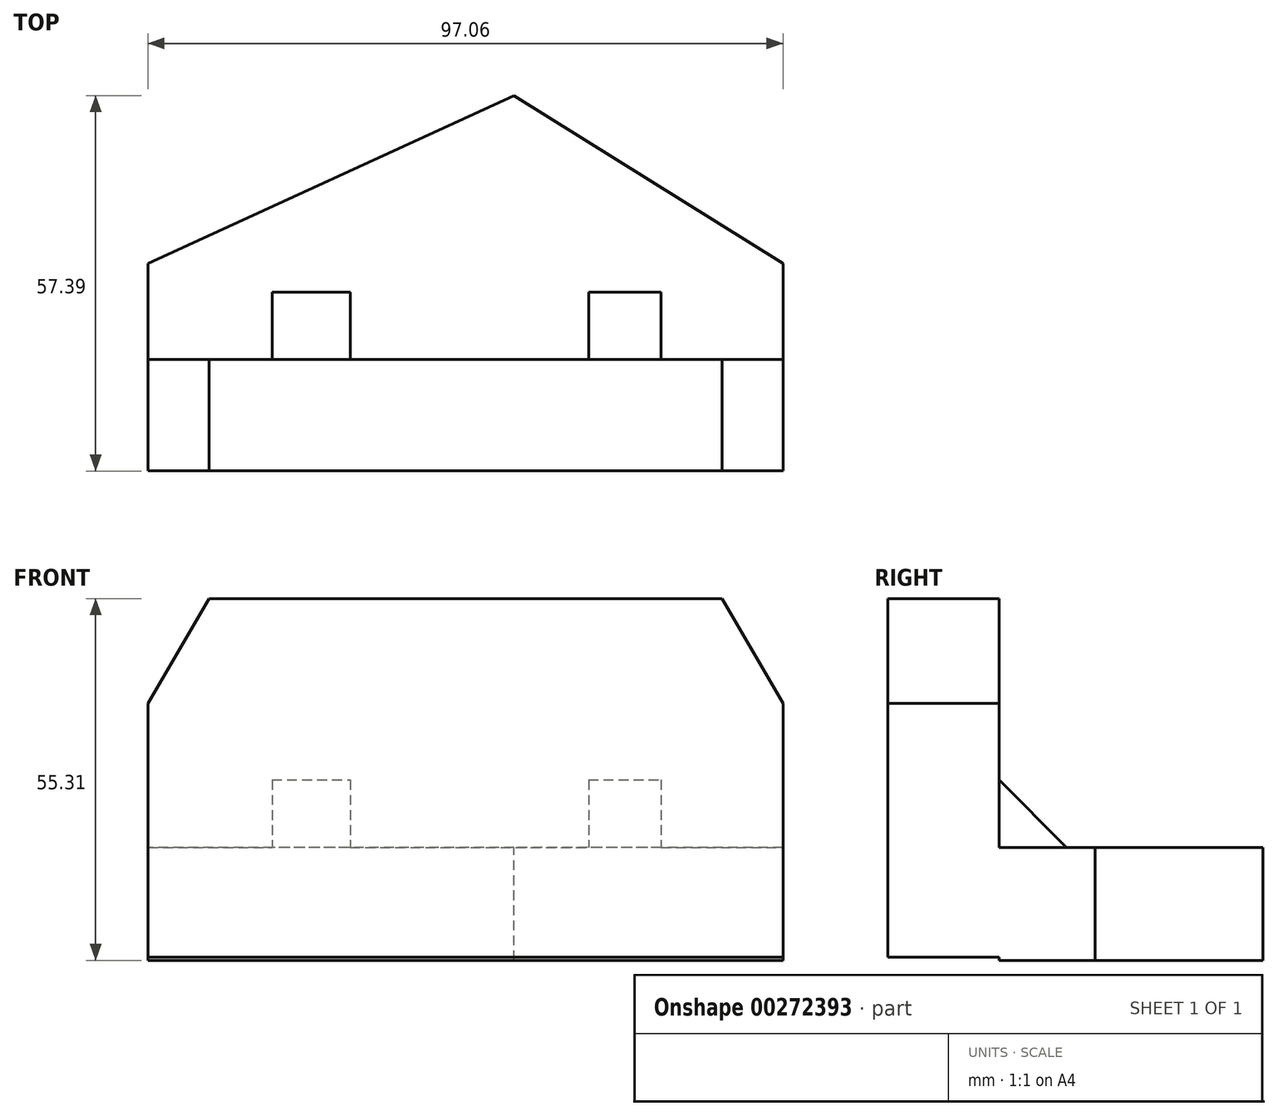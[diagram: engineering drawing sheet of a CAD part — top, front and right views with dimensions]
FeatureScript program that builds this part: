
annotation { "Feature Type Name" : "Feature", "Feature Type Description" : "" }
export const myFeature = defineFeature(function(context is Context, id is Id, definition is map)
    precondition{}
    {
        {
            var Q0;
            Q0=qCreatedBy(makeId("Front.planeOp"),FACE);
            var sketch = newSketch(context, id + "F0", { "sketchPlane" : qUnion([Q0])});
            skLineSegment(sketch, "E0", {"start": v(-58.59, -16.76) * mm, "end": v(-58.59, 22) * mm});
            skLineSegment(sketch, "E1", {"start": v(-58.59, 22) * mm, "end": v(-49.26, 38.04) * mm});
            skLineSegment(sketch, "E2", {"start": v(-49.26, 38.04) * mm, "end": v(29.15, 38.04) * mm});
            skLineSegment(sketch, "E3", {"start": v(29.15, 38.04) * mm, "end": v(38.47, 22) * mm});
            skLineSegment(sketch, "E4", {"start": v(38.47, 22) * mm, "end": v(38.47, -16.76) * mm});
            skLineSegment(sketch, "E5", {"start": v(-58.59, -16.76) * mm, "end": v(38.47, -16.76) * mm});
            skSolve(sketch);
        }
        {
            var Q0;
            Q0 = qSketchRegion(id + "F0", true);
            extrude(context, id + "F1", {"entities" : qUnion([Q0]), "depth" : 17.02 * mm});
        }
        {
            var Q0;
            Q0=qCreatedBy(makeId("Top.planeOp"),FACE);
            var sketch = newSketch(context, id + "F2", { "sketchPlane" : qUnion([Q0])});
            skLineSegment(sketch, "E6", {"start": v(-58.59, 0) * mm, "end": v(-58.59, 14.72) * mm});
            skLineSegment(sketch, "E7", {"start": v(38.47, 0) * mm, "end": v(38.47, 14.72) * mm});
            skLineSegment(sketch, "E8", {"start": v(38.47, 14.72) * mm, "end": v(-2.62, 40.37) * mm});
            skLineSegment(sketch, "E9", {"start": v(-2.62, 40.37) * mm, "end": v(-58.59, 14.72) * mm});
            skLineSegment(sketch, "E10", {"start": v(-58.59, 0) * mm, "end": v(38.47, 0) * mm});
            skSolve(sketch);
        }
        {
            var Q0;
            Q0 = qSketchRegion(id + "F2", true);
            extrude(context, id + "F3", {"entities" : qUnion([Q0]), "operationType" : NewBodyOperationType.ADD, "oppositeDirection" : true, "depth" : 17.27 * mm});
        }
        {
            var Q0;
            Q0=makeQuery(id+"F1.opExtrude","CAP_FACE",FACE,{"disambiguationData":[OSD([sQuery(id+"F0.wireOp",EDGE,"E0"),sQuery(id+"F0.wireOp",EDGE,"E1"),sQuery(id+"F0.wireOp",EDGE,"E2"),sQuery(id+"F0.wireOp",EDGE,"E3"),sQuery(id+"F0.wireOp",EDGE,"E4"),sQuery(id+"F0.wireOp",EDGE,"E5")])],"isStart":true});
            var sketch = newSketch(context, id + "F4", { "sketchPlane" : qUnion([Q0])});
            skLineSegment(sketch, "E11.bottom", {"start": v(-19.82, 15.89) * mm, "end": v(-8.74, 15.89) * mm});
            skLineSegment(sketch, "E11.top", {"start": v(-19.82, 0) * mm, "end": v(-8.74, 0) * mm});
            skLineSegment(sketch, "E11.left", {"start": v(-19.82, 15.89) * mm, "end": v(-19.82, 0) * mm});
            skLineSegment(sketch, "E11.right", {"start": v(-8.74, 15.89) * mm, "end": v(-8.74, 0) * mm});
            skLineSegment(sketch, "E12.bottom", {"start": v(27.7, 15.89) * mm, "end": v(39.64, 15.89) * mm});
            skLineSegment(sketch, "E12.top", {"start": v(27.7, 0) * mm, "end": v(39.64, 0) * mm});
            skLineSegment(sketch, "E12.left", {"start": v(27.7, 15.89) * mm, "end": v(27.7, 0) * mm});
            skLineSegment(sketch, "E12.right", {"start": v(39.64, 15.89) * mm, "end": v(39.64, 0) * mm});
            skSolve(sketch);
        }
        {
            var Q0;
            Q0 = qSketchRegion(id + "F4", true);
            extrude(context, id + "F5", {"entities" : qUnion([Q0]), "operationType" : NewBodyOperationType.ADD, "depth" : 19.8 * mm});
        }
        {
            var Q0;
            Q0=makeQuery(id+"F5.opExtrude","CAP_EDGE",EDGE,{"disambiguationData":[OSD([sQuery(id+"F4.wireOp",EDGE,"E11.bottom")])],"isStart":false});
            chamfer(context, id + "F6", {"entities" : qUnion([Q0]), "width" : 25.4 * mm, "tangentPropagation" : true});
        }
        {
            var Q0;
            Q0=makeQuery(id+"F5.opExtrude","CAP_EDGE",EDGE,{"disambiguationData":[OSD([sQuery(id+"F4.wireOp",EDGE,"E12.bottom")])],"isStart":false});
            chamfer(context, id + "F7", {"entities" : qUnion([Q0]), "width" : 25.4 * mm, "tangentPropagation" : true});
        }
    });
